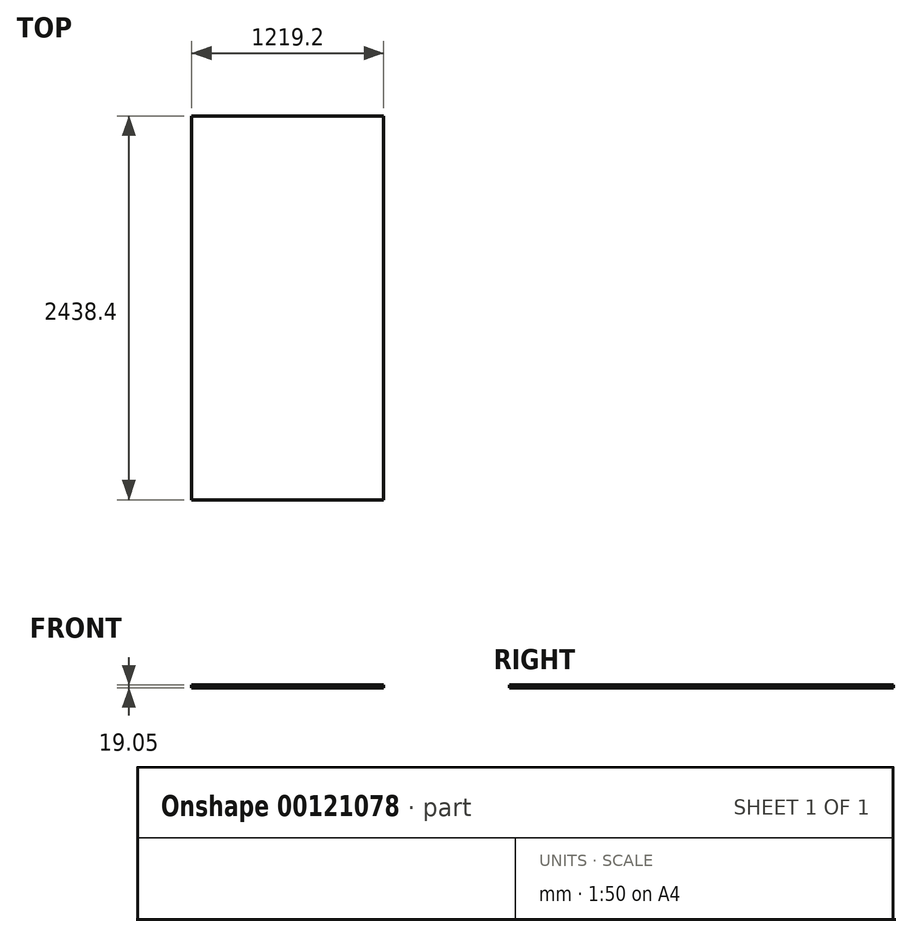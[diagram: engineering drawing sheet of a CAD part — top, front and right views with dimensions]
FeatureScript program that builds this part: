
annotation { "Feature Type Name" : "Feature", "Feature Type Description" : "" }
export const myFeature = defineFeature(function(context is Context, id is Id, definition is map)
    precondition{}
    {
        {
            var Q0;
            Q0=qCreatedBy(makeId("Top.planeOp"),FACE);
            var sketch = newSketch(context, id + "F0", { "sketchPlane" : qUnion([Q0])});
            skLineSegment(sketch, "E0.bottom", {"start": v(609.6, -1219.2) * mm, "end": v(-609.6, -1219.2) * mm});
            skLineSegment(sketch, "E0.top", {"start": v(609.6, 1219.2) * mm, "end": v(-609.6, 1219.2) * mm});
            skLineSegment(sketch, "E0.left", {"start": v(609.6, -1219.2) * mm, "end": v(609.6, 1219.2) * mm});
            skLineSegment(sketch, "E0.right", {"start": v(-609.6, -1219.2) * mm, "end": v(-609.6, 1219.2) * mm});
            skPoint(sketch, "E0.middle", {"position": v(0, 0) * mm});
            skSolve(sketch);
        }
        {
            var Q0;
            Q0 = qSketchRegion(id + "F0", true);
            extrude(context, id + "F1", {"entities" : qUnion([Q0]), "depth" : 19.05 * mm});
        }
    });
